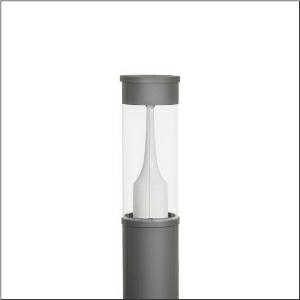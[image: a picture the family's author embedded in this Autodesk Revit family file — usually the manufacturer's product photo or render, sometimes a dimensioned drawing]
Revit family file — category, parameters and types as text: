
# Revit family: city-light_120_iq___pl1_2s_5xa5285cf14h_ce3b
name_source: partatom
category: Lighting Fixtures
units: mm (PartAtom-declared; Revit-internal decimal feet)

## family parameters
Cut with Voids When Loaded = No
Host = Face
Light Source = No
Part Type = Normal
Room Calculation Point = No
Round Connector Dimension = Use Diameter
Shared = No

## types (1)
- --- (1 x LED, 2970 lm, 23.9 W, 2200K)
    Apparent Load = 24 VA
    CIE Flux Codes = 23 62 94 96 100
    Color Rendering = 70
    Color Temperature = 2200K
    Default Elevation = 1800 mm
    Description = City-Light 120 iQ, bollard luminaire, Module 540 iQ-SR, primary light control with 3 zone facetted reflector, of plastic, silver coated, highly specular, structured, primary optical cover: cover, of PMMA, transparent, partly coated, light distribution: PL1.2s, primary light characteristic: symmetric, LED, High Power LED, rated luminous flux: 2.970lm, luminous efficacy: 124lm/W, light colour: 722, colour temperature: 2200K, control gear: iQ Street-Remote, control: pre-setting: logarithmic dimming characteristic, Street-Remote, Auto-Match, Temp-Guard, Lumen-Switch, Night-Set, Smart-Wire, Light-Fading, Desk-Remote (wireless, voltage-free reading and setting of iQ features in the workshop via application-optimized NFC function/RFID function), optimised constant luminous flux control (CLO 2.0), with terminal, 6-pole, max. 2.5mm², mains connection: 230..240V, AC, 50/60Hz, start of lifetime: 24W, end of service life: 26W, reduction: 12W, luminaire housing, cylindrical, of extruded aluminium section, coated, Siteco® metallic grey (DB 702S), length: 1.200mm, diameter: 200mm, Module 540 iQ-SR, traffic white (RAL 9016), equipment: standard, protection rating (complete): IP54, insulation class (complete): insulation class II (safety insulation), certification: CE, ENEC, VDE, packaging unit: 1 piece

Light Distribution: PL1.2s
    Height = 500 mm
    Lamp = 1 x LED
    Lamp Light Flux = 2970 lm
    Lamp Power = 23.9 W
    Lamp count = 1
    Length = 200 mm
    Luminous efficacy = 124 lm/W
    Manufacturer = Siteco
    ModVariant = No
    Model = 5XA5285CF14H
    Mounting Place = Floor
    Mounting Type = Freestanding
    Number of Poles = 1
    OnlyDefault = Yes
    Power Factor = 1
    Product Name = City-Light 120 iQ | PL1.2s
    Product group = bollard luminaire
    ProductGroupID = 1304
    Protection Class = Protection class II
    Protection Degree = IP 54
    RLX_Detail_Level = 1
    RLX_Emergency_Light_Flux = 0 lm
    RLX_Emergency_Type = 0
    RLX_Emergency_Type_DB = No
    RlxData = <blob elided: 22461 chars, md5=a4fedbe2>
    Socket = socket
    Standby Power = 0 W
    System Light Flux = 2970 lm
    System Power = 24 W
    Type Comments = factory setting: luminous flux: 100 % | dim-lin: 254 | 499 mA
    Type Image = l_1006922.jpg
    URL = http://relux.com
    VarID = @adj_166709
    Voltage = 0 V
    Weight = 0.00 kg
    Width = 0 mm  [stored 0 ft]

note: [stored X ft] marks values corroborated as IEEE doubles in the binary element streams (Revit-internal decimal feet)

## geometry (parser evidence)
native form markers: Blend x4, Sweep x10
no freeform markers — native parametric forms only
